# Revit family: P300330-009
name_source: partatom
category: Lighting Fixtures
revit_build: Autodesk Revit 2017 (Build: 20160225_1515(x64)
units: mm (PartAtom-declared; Revit-internal decimal feet)

## family parameters
Cut with Voids When Loaded = No
Host = Face
Light Source = No
OmniClass Number = 23.80.70.11.14.17
OmniClass Title = Direct/Indirect
Part Type = Normal
Room Calculation Point = No
Round Connector Dimension = Use Diameter
Shared = Yes

## types (1)
- P300328-009
    Apparent Load = 100 VA
    Assembly Code = D5020200
    Connector Description = Lighting Connector
    Default Elevation = 48 "
    Description = Merry Collection Four-Light Brushed Nickel and Etched Glass Transitional Style Bath Vanity Wall Light
    Features = Incorporate a clean, contemporary design with the Merry Collection 4-Light Etched Glass Brushed Nickel Transitional Bath Vanity Light. Light sources glow from within crisp etched glass shades for a generous elegant glow sure to transform any bath into a modern retreat. The rectangular backplate, curved arms, and round light bases are coated in a beautiful brushed nickel finish that perfectly blends transitional and modern character.
Application: Ideal for any bathroom.
Style: Perfect for modern and transitional style settings.
Finish: The rectangular backplate, curved arms, and round light bases are coated in a beautiful brushed nickel finish that perfectly blends transitional and modern character.
Materials: Constructed from steel to ensure a long product lifespan.
Glass: Light sources glow from within crisp etched glass shades for a generous elegant glow sure to transform any bath into a modern retreat.
Bulbs: For ideal illumination, use 4 medium base bulbs that are sold separately (100w max - LED/CFL/incandescent). Compatible with dimmable bulbs.
Dimensions: Measures 30-inch length by 8.25-inch height by 5.75-inch depth (installed).
Certifications: cULus damp location listed.
Pairs With: Pairs with Progress Lighting fixtures from the Tobin, Etched Glass Flush, and Dome Glass collections.
Warranty: Our 1-Year Limited Warranty guarantees your complete satisfaction with your purchase and includes professional after-sales customer service support. Make your purchase today to breathe new life into your lighting design!
    Glass = Paint - Hubbell - White Texture
    Housing Material = Paint - Hubbell - Metallic Silver Textured
    Lamp = LED/CFL/incandescent
    Load Classification = Lighting
    Manufacturer = Progress Lighting
    Model = P300330-009
    Power Factor = 1
    Product Documentation Link = https://hubbellcdn.com
    Product Link = https://www.hubbell.com
    URL = https://www.hubbell.com
    Voltage = 120 V
    Warranty = 1 year Warranty
    Wattage Comments = 100W
    Watts = 100 W

## geometry (parser evidence)
native form markers: Sweep x6
no freeform markers — native parametric forms only
